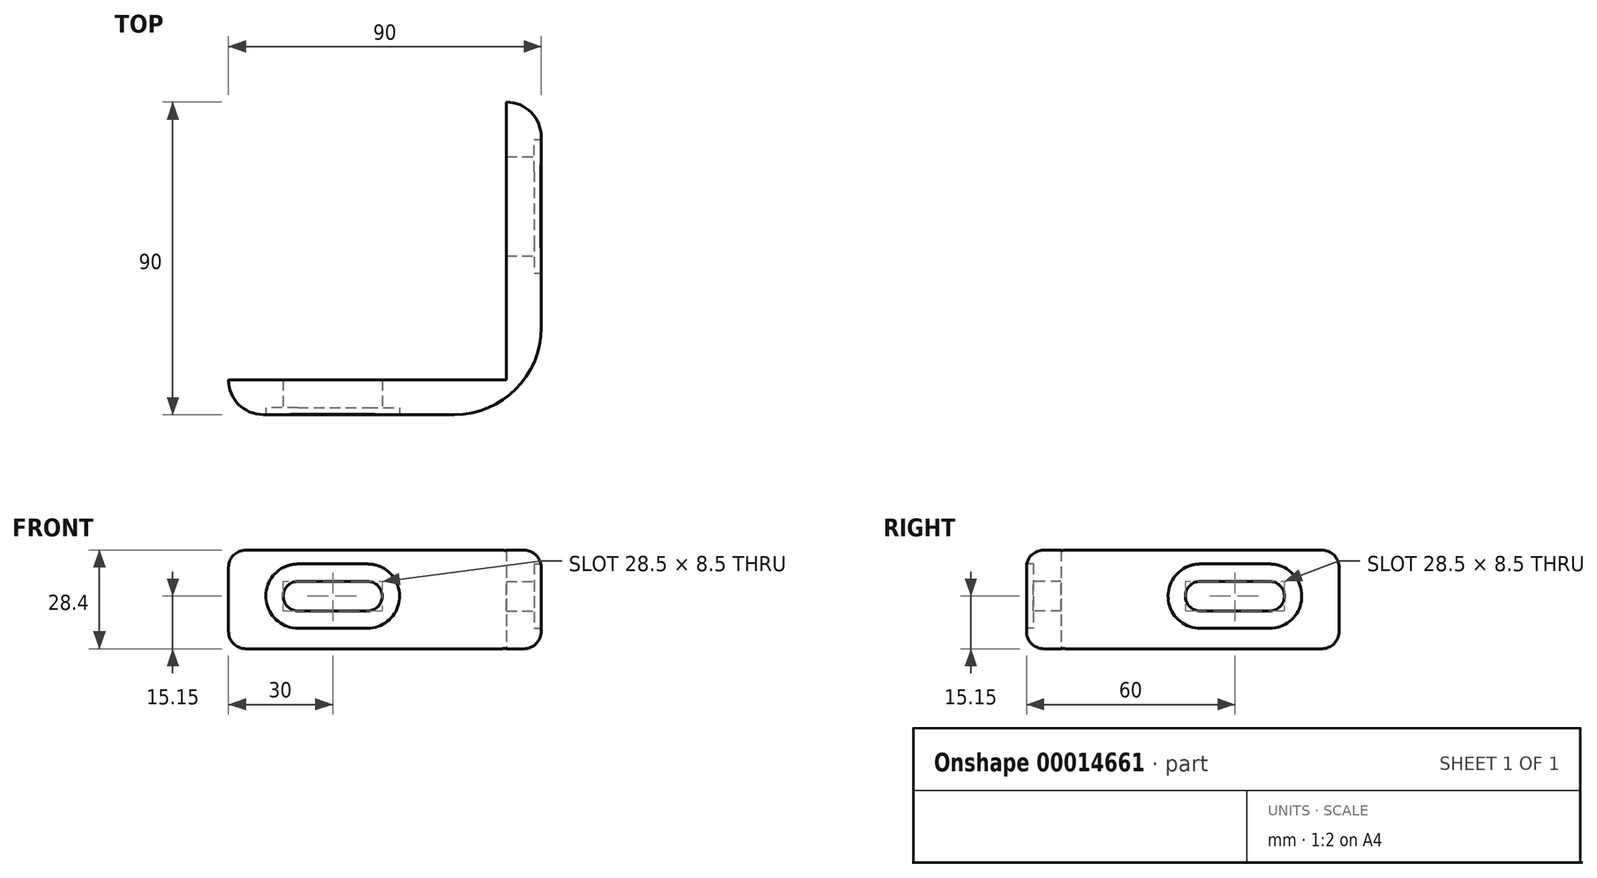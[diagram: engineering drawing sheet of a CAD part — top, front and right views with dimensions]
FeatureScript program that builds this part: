
annotation { "Feature Type Name" : "Feature", "Feature Type Description" : "" }
export const myFeature = defineFeature(function(context is Context, id is Id, definition is map)
    precondition{}
    {
        {
            var Q0;
            Q0=qCreatedBy(makeId("Top.planeOp"),FACE);
            var sketch = newSketch(context, id + "F0", { "sketchPlane" : qUnion([Q0])});
            skLineSegment(sketch, "E0", {"start": v(0, 0) * mm, "end": v(-80, 0) * mm});
            skLineSegment(sketch, "E1", {"start": v(0, 0) * mm, "end": v(0, 80) * mm});
            skLineSegment(sketch, "E2", {"start": v(-80, 0) * mm, "end": v(-80, -10) * mm});
            skLineSegment(sketch, "E3", {"start": v(-80, -10) * mm, "end": v(10, -10) * mm});
            skLineSegment(sketch, "E4", {"start": v(10, -10) * mm, "end": v(10, 80) * mm});
            skLineSegment(sketch, "E5", {"start": v(10, 80) * mm, "end": v(0, 80) * mm});
            skSolve(sketch);
        }
        {
            var Q0;
            Q0 = qSketchRegion(id + "F0", true);
            extrude(context, id + "F1", {"entities" : qUnion([Q0]), "depth" : 28.4 * mm});
        }
        {
            var Q0;
            Q0=makeQuery(id+"F1.opExtrude","SWEPT_EDGE",EDGE,{"disambiguationData":[OSD([sQuery(id+"F0.wireOp",EDGE,"E2"),sQuery(id+"F0.wireOp",EDGE,"E3")])]});
            var Q1;
            Q1=makeQuery(id+"F1.opExtrude","SWEPT_EDGE",EDGE,{"disambiguationData":[OSD([sQuery(id+"F0.wireOp",EDGE,"E4"),sQuery(id+"F0.wireOp",EDGE,"E5")])]});
            fillet(context, id + "F2", {"entities" : qUnion([Q0, Q1]), "radius" : 10 * mm, "tangentPropagation" : true, "allowEdgeOverflow" : false});
        }
        {
            var Q0;
            Q0=makeQuery(id+"F1.opExtrude","SWEPT_EDGE",EDGE,{"disambiguationData":[OSD([sQuery(id+"F0.wireOp",EDGE,"E3"),sQuery(id+"F0.wireOp",EDGE,"E4")])]});
            fillet(context, id + "F3", {"entities" : qUnion([Q0]), "radius" : 25 * mm, "tangentPropagation" : true, "allowEdgeOverflow" : false});
        }
        {
            var Q0;
            Q0=makeQuery(id+"F1.opExtrude","SWEPT_FACE",FACE,{"disambiguationData":[OSD([sQuery(id+"F0.wireOp",EDGE,"E3")])]});
            var sketch = newSketch(context, id + "F4", { "sketchPlane" : qUnion([Q0])});
            skLineSegment(sketch, "E6.0", {"start": v(0, 28.4) * mm, "end": v(-80, 28.4) * mm, "construction": true});
            skLineSegment(sketch, "E7.0", {"start": v(0, 28.4) * mm, "end": v(0, 0) * mm, "construction": true});
            skLineSegment(sketch, "E8", {"start": v(-60, 19.4) * mm, "end": v(-40, 19.4) * mm});
            skLineSegment(sketch, "E9", {"start": v(-40, 10.9) * mm, "end": v(-60, 10.9) * mm});
            skArc(sketch, "E10", {"start": v(-40, 19.4) * mm, "mid": v(-35.75, 15.15) * mm, "end": v(-40, 10.9) * mm});
            skArc(sketch, "E11", {"start": v(-60, 19.4) * mm, "mid": v(-64.25, 15.15) * mm, "end": v(-60, 10.9) * mm});
            skSolve(sketch);
        }
        {
            var Q0;
            Q0=makeQuery(id+"F4.imprint","IMPRINT",FACE,{"disambiguationData":[TD([[makeQuery(id+"F4.imprint","IMPRINT",EDGE,{"derivedFrom":sQuery(id+"F4.wireOp",EDGE,"E8")}),-1.0]])]});
            extrude(context, id + "F5", {"entities" : qUnion([Q0]), "operationType" : NewBodyOperationType.REMOVE, "endBound" : BoundingType.UP_TO_NEXT, "oppositeDirection" : true, "depth" : 25 * mm});
        }
        {
            var Q0;
            Q0=makeQuery(id+"F1.opExtrude","SWEPT_FACE",FACE,{"disambiguationData":[OSD([sQuery(id+"F0.wireOp",EDGE,"E4")])]});
            var sketch = newSketch(context, id + "F6", { "sketchPlane" : qUnion([Q0])});
            skLineSegment(sketch, "E12.0", {"start": v(0, 28.4) * mm, "end": v(0, 0) * mm, "construction": true});
            skLineSegment(sketch, "E13.0", {"start": v(0, 28.4) * mm, "end": v(80, 28.4) * mm, "construction": true});
            skLineSegment(sketch, "E14", {"start": v(40, 19.4) * mm, "end": v(60, 19.4) * mm});
            skLineSegment(sketch, "E15", {"start": v(60, 10.9) * mm, "end": v(40, 10.9) * mm});
            skArc(sketch, "E16", {"start": v(40, 19.4) * mm, "mid": v(35.75, 15.15) * mm, "end": v(40, 10.9) * mm});
            skArc(sketch, "E17", {"start": v(60, 19.4) * mm, "mid": v(64.25, 15.15) * mm, "end": v(60, 10.9) * mm});
            skSolve(sketch);
        }
        {
            var Q0;
            Q0=makeQuery(id+"F6.imprint","IMPRINT",FACE,{"disambiguationData":[TD([[makeQuery(id+"F6.imprint","IMPRINT",EDGE,{"derivedFrom":sQuery(id+"F6.wireOp",EDGE,"E14")}),-1.0]])]});
            extrude(context, id + "F7", {"entities" : qUnion([Q0]), "operationType" : NewBodyOperationType.REMOVE, "endBound" : BoundingType.UP_TO_NEXT, "oppositeDirection" : true, "depth" : 25 * mm});
        }
        {
            var Q0;
            Q0=makeQuery(id+"F1.opExtrude","SWEPT_FACE",FACE,{"disambiguationData":[OSD([sQuery(id+"F0.wireOp",EDGE,"E3")])]});
            var sketch = newSketch(context, id + "F8", { "sketchPlane" : qUnion([Q0])});
            skArc(sketch, "E18.0", {"start": v(-40, 19.4) * mm, "mid": v(-35.75, 15.15) * mm, "end": v(-40, 10.9) * mm, "construction": true});
            skLineSegment(sketch, "E19.0", {"start": v(-60, 19.4) * mm, "end": v(-40, 19.4) * mm, "construction": true});
            skArc(sketch, "E20.0", {"start": v(-60, 19.4) * mm, "mid": v(-64.25, 15.15) * mm, "end": v(-60, 10.9) * mm, "construction": true});
            skLineSegment(sketch, "E21.0", {"start": v(-40, 10.9) * mm, "end": v(-60, 10.9) * mm, "construction": true});
            skLineSegment(sketch, "E22.0", {"start": v(-60, 24.4) * mm, "end": v(-40, 24.4) * mm});
            skArc(sketch, "E22.1", {"start": v(-60, 24.4) * mm, "mid": v(-69.25, 15.15) * mm, "end": v(-60, 5.9) * mm});
            skLineSegment(sketch, "E22.2", {"start": v(-40, 5.9) * mm, "end": v(-60, 5.9) * mm});
            skArc(sketch, "E22.3", {"start": v(-40, 24.4) * mm, "mid": v(-30.75, 15.15) * mm, "end": v(-40, 5.9) * mm});
            skSolve(sketch);
        }
        {
            var Q0;
            Q0 = qSketchRegion(id + "F8", true);
            extrude(context, id + "F9", {"entities" : qUnion([Q0]), "operationType" : NewBodyOperationType.REMOVE, "oppositeDirection" : true, "depth" : 2 * mm});
        }
        {
            var Q0;
            Q0=makeQuery(id+"F1.opExtrude","SWEPT_FACE",FACE,{"disambiguationData":[OSD([sQuery(id+"F0.wireOp",EDGE,"E4")])]});
            var sketch = newSketch(context, id + "F10", { "sketchPlane" : qUnion([Q0])});
            skLineSegment(sketch, "E23.0", {"start": v(40, 19.4) * mm, "end": v(60, 19.4) * mm, "construction": true});
            skArc(sketch, "E24.0", {"start": v(60, 19.4) * mm, "mid": v(64.25, 15.15) * mm, "end": v(60, 10.9) * mm, "construction": true});
            skLineSegment(sketch, "E25.0", {"start": v(60, 10.9) * mm, "end": v(40, 10.9) * mm, "construction": true});
            skArc(sketch, "E26.0", {"start": v(40, 19.4) * mm, "mid": v(35.75, 15.15) * mm, "end": v(40, 10.9) * mm, "construction": true});
            skLineSegment(sketch, "E27.0", {"start": v(40, 24.4) * mm, "end": v(60, 24.4) * mm});
            skArc(sketch, "E27.1", {"start": v(40, 24.4) * mm, "mid": v(30.75, 15.15) * mm, "end": v(40, 5.9) * mm});
            skLineSegment(sketch, "E27.2", {"start": v(60, 5.9) * mm, "end": v(40, 5.9) * mm});
            skArc(sketch, "E27.3", {"start": v(60, 24.4) * mm, "mid": v(69.25, 15.15) * mm, "end": v(60, 5.9) * mm});
            skSolve(sketch);
        }
        {
            var Q0;
            Q0 = qSketchRegion(id + "F10", true);
            extrude(context, id + "F11", {"entities" : qUnion([Q0]), "operationType" : NewBodyOperationType.REMOVE, "oppositeDirection" : true, "depth" : 2 * mm});
        }
        {
            var Q0;
            {var subQ0=sQuery(id+"F0.wireOp",EDGE,"E2");var subQ1=sQuery(id+"F0.wireOp",EDGE,"E3");Q0=makeQuery(id+"F2.opFillet","BLEND_EDGE",EDGE,{"blendedFrom":[makeQuery(id+"F1.opExtrude","SWEPT_EDGE",EDGE,{"disambiguationData":[OSD([subQ0,subQ1])]}),makeQuery(id+"F1.opExtrude","CAP_FACE",FACE,{"disambiguationData":[OSD([sQuery(id+"F0.wireOp",EDGE,"E0"),sQuery(id+"F0.wireOp",EDGE,"E1"),subQ0,subQ1,sQuery(id+"F0.wireOp",EDGE,"E4"),sQuery(id+"F0.wireOp",EDGE,"E5")])],"isStart":false})],"blendedInto":[makeQuery(id+"F1.opExtrude","CAP_FACE",FACE,{"disambiguationData":[OSD([sQuery(id+"F0.wireOp",EDGE,"E0"),sQuery(id+"F0.wireOp",EDGE,"E1"),subQ0,subQ1,sQuery(id+"F0.wireOp",EDGE,"E4"),sQuery(id+"F0.wireOp",EDGE,"E5")])],"isStart":false})]});}
            var Q1;
            Q1=makeQuery(id+"F1.opExtrude","CAP_EDGE",EDGE,{"disambiguationData":[OSD([sQuery(id+"F0.wireOp",EDGE,"E3")])],"isStart":false});
            var Q2;
            {var subQ0=sQuery(id+"F0.wireOp",EDGE,"E3");var subQ1=sQuery(id+"F0.wireOp",EDGE,"E4");Q2=makeQuery(id+"F3.opFillet","BLEND_EDGE",EDGE,{"blendedFrom":[makeQuery(id+"F1.opExtrude","SWEPT_EDGE",EDGE,{"disambiguationData":[OSD([subQ0,subQ1])]}),makeQuery(id+"F1.opExtrude","CAP_FACE",FACE,{"disambiguationData":[OSD([sQuery(id+"F0.wireOp",EDGE,"E0"),sQuery(id+"F0.wireOp",EDGE,"E1"),sQuery(id+"F0.wireOp",EDGE,"E2"),subQ0,subQ1,sQuery(id+"F0.wireOp",EDGE,"E5")])],"isStart":false})],"blendedInto":[makeQuery(id+"F1.opExtrude","CAP_FACE",FACE,{"disambiguationData":[OSD([sQuery(id+"F0.wireOp",EDGE,"E0"),sQuery(id+"F0.wireOp",EDGE,"E1"),sQuery(id+"F0.wireOp",EDGE,"E2"),subQ0,subQ1,sQuery(id+"F0.wireOp",EDGE,"E5")])],"isStart":false})]});}
            var Q3;
            Q3=makeQuery(id+"F1.opExtrude","CAP_EDGE",EDGE,{"disambiguationData":[OSD([sQuery(id+"F0.wireOp",EDGE,"E4")])],"isStart":false});
            var Q4;
            {var subQ0=sQuery(id+"F0.wireOp",EDGE,"E4");var subQ1=sQuery(id+"F0.wireOp",EDGE,"E5");Q4=makeQuery(id+"F2.opFillet","BLEND_EDGE",EDGE,{"blendedFrom":[makeQuery(id+"F1.opExtrude","SWEPT_EDGE",EDGE,{"disambiguationData":[OSD([subQ0,subQ1])]}),makeQuery(id+"F1.opExtrude","CAP_FACE",FACE,{"disambiguationData":[OSD([sQuery(id+"F0.wireOp",EDGE,"E0"),sQuery(id+"F0.wireOp",EDGE,"E1"),sQuery(id+"F0.wireOp",EDGE,"E2"),sQuery(id+"F0.wireOp",EDGE,"E3"),subQ0,subQ1])],"isStart":false})],"blendedInto":[makeQuery(id+"F1.opExtrude","CAP_FACE",FACE,{"disambiguationData":[OSD([sQuery(id+"F0.wireOp",EDGE,"E0"),sQuery(id+"F0.wireOp",EDGE,"E1"),sQuery(id+"F0.wireOp",EDGE,"E2"),sQuery(id+"F0.wireOp",EDGE,"E3"),subQ0,subQ1])],"isStart":false})]});}
            fillet(context, id + "F12", {"entities" : qUnion([Q0, Q1, Q2, Q3, Q4]), "radius" : 5 * mm, "tangentPropagation" : true, "allowEdgeOverflow" : false});
        }
        {
            var Q0;
            {var subQ0=sQuery(id+"F0.wireOp",EDGE,"E2");var subQ1=sQuery(id+"F0.wireOp",EDGE,"E3");Q0=makeQuery(id+"F2.opFillet","BLEND_EDGE",EDGE,{"blendedFrom":[makeQuery(id+"F1.opExtrude","SWEPT_EDGE",EDGE,{"disambiguationData":[OSD([subQ0,subQ1])]}),makeQuery(id+"F1.opExtrude","CAP_FACE",FACE,{"disambiguationData":[OSD([sQuery(id+"F0.wireOp",EDGE,"E0"),sQuery(id+"F0.wireOp",EDGE,"E1"),subQ0,subQ1,sQuery(id+"F0.wireOp",EDGE,"E4"),sQuery(id+"F0.wireOp",EDGE,"E5")])],"isStart":true})],"blendedInto":[makeQuery(id+"F1.opExtrude","CAP_FACE",FACE,{"disambiguationData":[OSD([sQuery(id+"F0.wireOp",EDGE,"E0"),sQuery(id+"F0.wireOp",EDGE,"E1"),subQ0,subQ1,sQuery(id+"F0.wireOp",EDGE,"E4"),sQuery(id+"F0.wireOp",EDGE,"E5")])],"isStart":true})]});}
            var Q1;
            Q1=makeQuery(id+"F1.opExtrude","CAP_EDGE",EDGE,{"disambiguationData":[OSD([sQuery(id+"F0.wireOp",EDGE,"E3")])],"isStart":true});
            var Q2;
            {var subQ0=sQuery(id+"F0.wireOp",EDGE,"E3");var subQ1=sQuery(id+"F0.wireOp",EDGE,"E4");Q2=makeQuery(id+"F3.opFillet","BLEND_EDGE",EDGE,{"blendedFrom":[makeQuery(id+"F1.opExtrude","SWEPT_EDGE",EDGE,{"disambiguationData":[OSD([subQ0,subQ1])]}),makeQuery(id+"F1.opExtrude","CAP_FACE",FACE,{"disambiguationData":[OSD([sQuery(id+"F0.wireOp",EDGE,"E0"),sQuery(id+"F0.wireOp",EDGE,"E1"),sQuery(id+"F0.wireOp",EDGE,"E2"),subQ0,subQ1,sQuery(id+"F0.wireOp",EDGE,"E5")])],"isStart":true})],"blendedInto":[makeQuery(id+"F1.opExtrude","CAP_FACE",FACE,{"disambiguationData":[OSD([sQuery(id+"F0.wireOp",EDGE,"E0"),sQuery(id+"F0.wireOp",EDGE,"E1"),sQuery(id+"F0.wireOp",EDGE,"E2"),subQ0,subQ1,sQuery(id+"F0.wireOp",EDGE,"E5")])],"isStart":true})]});}
            var Q3;
            Q3=makeQuery(id+"F1.opExtrude","CAP_EDGE",EDGE,{"disambiguationData":[OSD([sQuery(id+"F0.wireOp",EDGE,"E4")])],"isStart":true});
            var Q4;
            {var subQ0=sQuery(id+"F0.wireOp",EDGE,"E4");var subQ1=sQuery(id+"F0.wireOp",EDGE,"E5");Q4=makeQuery(id+"F2.opFillet","BLEND_EDGE",EDGE,{"blendedFrom":[makeQuery(id+"F1.opExtrude","SWEPT_EDGE",EDGE,{"disambiguationData":[OSD([subQ0,subQ1])]}),makeQuery(id+"F1.opExtrude","CAP_FACE",FACE,{"disambiguationData":[OSD([sQuery(id+"F0.wireOp",EDGE,"E0"),sQuery(id+"F0.wireOp",EDGE,"E1"),sQuery(id+"F0.wireOp",EDGE,"E2"),sQuery(id+"F0.wireOp",EDGE,"E3"),subQ0,subQ1])],"isStart":true})],"blendedInto":[makeQuery(id+"F1.opExtrude","CAP_FACE",FACE,{"disambiguationData":[OSD([sQuery(id+"F0.wireOp",EDGE,"E0"),sQuery(id+"F0.wireOp",EDGE,"E1"),sQuery(id+"F0.wireOp",EDGE,"E2"),sQuery(id+"F0.wireOp",EDGE,"E3"),subQ0,subQ1])],"isStart":true})]});}
            fillet(context, id + "F13", {"entities" : qUnion([Q0, Q1, Q2, Q3, Q4]), "radius" : 5 * mm, "tangentPropagation" : true, "allowEdgeOverflow" : false});
        }
    });
